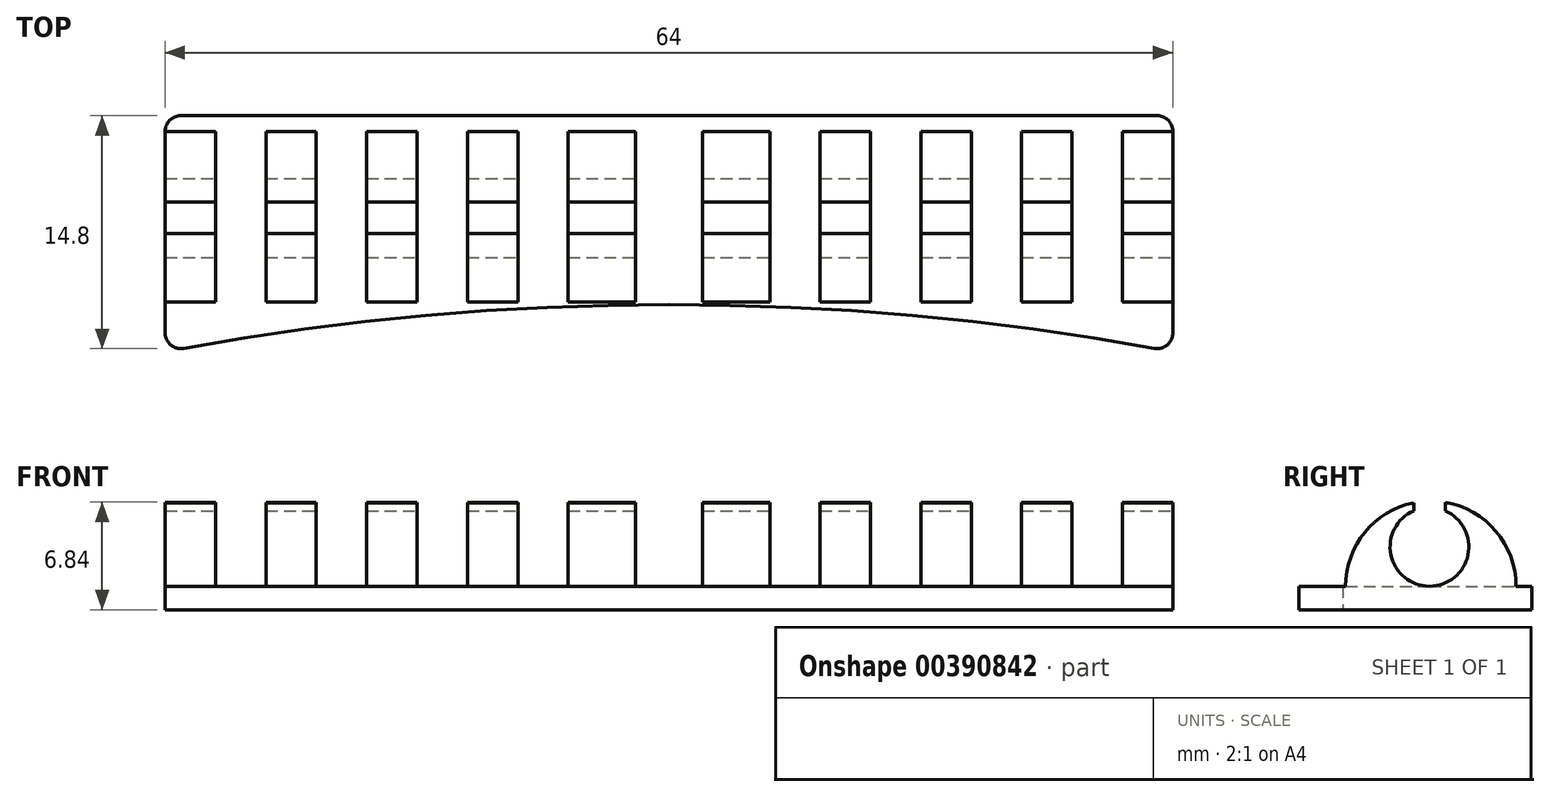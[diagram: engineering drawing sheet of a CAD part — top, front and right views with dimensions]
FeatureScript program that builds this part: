
annotation { "Feature Type Name" : "Feature", "Feature Type Description" : "" }
export const myFeature = defineFeature(function(context is Context, id is Id, definition is map)
    precondition{}
    {
        {
            var Q0;
            Q0=qCreatedBy(makeId("Top.planeOp"),FACE);
            var sketch = newSketch(context, id + "F0", { "sketchPlane" : qUnion([Q0])});
            skLineSegment(sketch, "E0.top", {"start": v(-32, 7.5) * mm, "end": v(32, 7.5) * mm});
            skLineSegment(sketch, "E0.left", {"start": v(-32, -7.5) * mm, "end": v(-32, 7.5) * mm});
            skLineSegment(sketch, "E0.right", {"start": v(32, -7.5) * mm, "end": v(32, 7.5) * mm});
            skPoint(sketch, "E0.middle", {"position": v(0, 0) * mm});
            skArc(sketch, "E1", {"start": v(32, -7.5) * mm, "mid": v(0, -4.5) * mm, "end": v(-32, -7.5) * mm});
            skSolve(sketch);
        }
        {
            var Q0;
            Q0 = qSketchRegion(id + "F0", true);
            extrude(context, id + "F1", {"entities" : qUnion([Q0]), "depth" : 1.5 * mm});
        }
        {
            var Q0;
            Q0=makeQuery(id+"F1.opExtrude","SWEPT_EDGE",EDGE,{"disambiguationData":[OSD([sQuery(id+"F0.wireOp",EDGE,"E0.top"),sQuery(id+"F0.wireOp",EDGE,"E0.right")])]});
            var Q1;
            Q1=makeQuery(id+"F1.opExtrude","SWEPT_EDGE",EDGE,{"disambiguationData":[OSD([sQuery(id+"F0.wireOp",EDGE,"E0.right"),sQuery(id+"F0.wireOp",EDGE,"E1")])]});
            var Q2;
            Q2=makeQuery(id+"F1.opExtrude","SWEPT_EDGE",EDGE,{"disambiguationData":[OSD([sQuery(id+"F0.wireOp",EDGE,"E0.left"),sQuery(id+"F0.wireOp",EDGE,"E1")])]});
            var Q3;
            Q3=makeQuery(id+"F1.opExtrude","SWEPT_EDGE",EDGE,{"disambiguationData":[OSD([sQuery(id+"F0.wireOp",EDGE,"E0.top"),sQuery(id+"F0.wireOp",EDGE,"E0.left")])]});
            fillet(context, id + "F2", {"entities" : qUnion([Q0, Q1, Q2, Q3]), "radius" : 1 * mm, "tangentPropagation" : true, "allowEdgeOverflow" : false});
        }
        {
            var Q0;
            Q0=makeQuery(id+"F1.opExtrude","SWEPT_FACE",FACE,{"disambiguationData":[OSD([sQuery(id+"F0.wireOp",EDGE,"E0.right")])]});
            var sketch = newSketch(context, id + "F3", { "sketchPlane" : qUnion([Q0])});
            skArc(sketch, "E2", {"start": v(0, 6.3) * mm, "mid": v(1, 1.5) * mm, "end": v(2, 6.3) * mm});
            skArc(sketch, "E3", {"start": v(6.5, 1.5) * mm, "mid": v(5.22, 5) * mm, "end": v(2, 6.84) * mm});
            skArc(sketch, "E4", {"start": v(0, 6.8) * mm, "mid": v(-3.1, 4.92) * mm, "end": v(-4.33, 1.5) * mm});
            skLineSegment(sketch, "E5.left", {"start": v(0, 6.3) * mm, "end": v(0, 6.8) * mm});
            skLineSegment(sketch, "E5.right", {"start": v(2, 6.3) * mm, "end": v(2, 6.84) * mm});
            skSolve(sketch);
        }
        {
            var Q0;
            {var subQ4=sQuery(id+"F3.wireOp",EDGE,"E4");Q0=makeQuery(id+"F3.imprint","IMPRINT",FACE,{"disambiguationData":[TD([[makeQuery(id+"F3.imprint","IMPRINT",EDGE,{"derivedFrom":subQ4}),1.0]])]});}
            var Q1;
            {var subQ5=sQuery(id+"F3.wireOp",EDGE,"E3");Q1=makeQuery(id+"F3.imprint","IMPRINT",FACE,{"disambiguationData":[TD([[makeQuery(id+"F3.imprint","IMPRINT",EDGE,{"derivedFrom":subQ5}),1.0]])]});}
            extrude(context, id + "F4", {"entities" : qUnion([Q0, Q1]), "operationType" : NewBodyOperationType.ADD, "oppositeDirection" : true, "depth" : 64 * mm});
        }
        {
            var Q0;
            {var subQ0=sQuery(id+"F0.wireOp",EDGE,"E1");var subQ1=sQuery(id+"F0.wireOp",EDGE,"E0.right");var subQ2=sQuery(id+"F0.wireOp",EDGE,"E0.left");Q0=makeQuery(id+"F4.boolean.opBoolean","SPLIT",FACE,{"disambiguationData":[TD([makeQuery(id+"F1.opExtrude","SWEPT_FACE",FACE,{"disambiguationData":[OSD([subQ0])]})])],"derivedFrom":makeQuery(id+"F1.opExtrude","CAP_FACE",FACE,{"disambiguationData":[OSD([sQuery(id+"F0.wireOp",EDGE,"E0.top"),subQ2,subQ1,subQ0])],"isStart":false})});}
            var sketch = newSketch(context, id + "F5", { "sketchPlane" : qUnion([Q0])});
            skLineSegment(sketch, "E6.bottom", {"start": v(-32, -4.33) * mm, "end": v(32, -4.33) * mm});
            skLineSegment(sketch, "E6.top", {"start": v(-32, 9.34) * mm, "end": v(32, 9.34) * mm});
            skLineSegment(sketch, "E6.left", {"start": v(-32, -4.33) * mm, "end": v(-32, 9.34) * mm});
            skLineSegment(sketch, "E6.right", {"start": v(32, -4.33) * mm, "end": v(32, 9.34) * mm});
            skLineSegment(sketch, "E7", {"start": v(28.8, -4.33) * mm, "end": v(28.8, 9.34) * mm});
            skLineSegment(sketch, "E8", {"start": v(25.6, -4.33) * mm, "end": v(25.6, 9.34) * mm});
            skLineSegment(sketch, "E9", {"start": v(22.4, -4.33) * mm, "end": v(22.4, 9.34) * mm});
            skLineSegment(sketch, "E10", {"start": v(19.2, -4.33) * mm, "end": v(19.2, 9.34) * mm});
            skLineSegment(sketch, "E11", {"start": v(16, -4.33) * mm, "end": v(16, 9.34) * mm});
            skLineSegment(sketch, "E12", {"start": v(12.8, -4.33) * mm, "end": v(12.8, 9.34) * mm});
            skLineSegment(sketch, "E13", {"start": v(9.6, -4.33) * mm, "end": v(9.6, 9.34) * mm});
            skLineSegment(sketch, "E14", {"start": v(6.4, 9.34) * mm, "end": v(6.4, -4.33) * mm});
            skLineSegment(sketch, "E15", {"start": v(-6.4, -4.33) * mm, "end": v(-6.4, 9.34) * mm});
            skLineSegment(sketch, "E16", {"start": v(-9.6, 9.34) * mm, "end": v(-9.6, -4.33) * mm});
            skLineSegment(sketch, "E17", {"start": v(-12.8, 9.34) * mm, "end": v(-12.8, -4.33) * mm});
            skLineSegment(sketch, "E18", {"start": v(-16, 9.34) * mm, "end": v(-16, -4.33) * mm});
            skLineSegment(sketch, "E19", {"start": v(-19.2, 9.34) * mm, "end": v(-19.2, -4.33) * mm});
            skLineSegment(sketch, "E20", {"start": v(-22.4, -4.33) * mm, "end": v(-22.4, 9.34) * mm});
            skLineSegment(sketch, "E21", {"start": v(-25.6, 9.34) * mm, "end": v(-25.6, -4.33) * mm});
            skLineSegment(sketch, "E22", {"start": v(-28.8, -4.33) * mm, "end": v(-28.8, 9.34) * mm});
            skLineSegment(sketch, "E23", {"start": v(-2.13, 9.34) * mm, "end": v(-2.13, -4.33) * mm});
            skLineSegment(sketch, "E24", {"start": v(-6.4, 9.34) * mm, "end": v(-6.4, -4.33) * mm});
            skLineSegment(sketch, "E25", {"start": v(2.13, -4.33) * mm, "end": v(2.13, 9.34) * mm});
            skSolve(sketch);
        }
        {
            var Q0;
            {var subQ0=sQuery(id+"F5.wireOp",EDGE,"E23");Q0=makeQuery(id+"F5.imprint","IMPRINT",FACE,{"disambiguationData":[TD([[makeQuery(id+"F5.imprint","IMPRINT",EDGE,{"derivedFrom":subQ0}),1.0]])]});}
            var Q1;
            {var subQ0=sQuery(id+"F5.wireOp",EDGE,"E16");Q1=makeQuery(id+"F5.imprint","IMPRINT",FACE,{"disambiguationData":[TD([[makeQuery(id+"F5.imprint","IMPRINT",EDGE,{"derivedFrom":subQ0}),1.0]])]});}
            var Q2;
            {var subQ0=sQuery(id+"F5.wireOp",EDGE,"E17");Q2=makeQuery(id+"F5.imprint","IMPRINT",FACE,{"disambiguationData":[TD([[makeQuery(id+"F5.imprint","IMPRINT",EDGE,{"derivedFrom":subQ0}),-1.0]])]});}
            var Q3;
            {var subQ0=sQuery(id+"F5.wireOp",EDGE,"E19");Q3=makeQuery(id+"F5.imprint","IMPRINT",FACE,{"disambiguationData":[TD([[makeQuery(id+"F5.imprint","IMPRINT",EDGE,{"derivedFrom":subQ0}),-1.0]])]});}
            var Q4;
            {var subQ0=sQuery(id+"F5.wireOp",EDGE,"E21");Q4=makeQuery(id+"F5.imprint","IMPRINT",FACE,{"disambiguationData":[TD([[makeQuery(id+"F5.imprint","IMPRINT",EDGE,{"derivedFrom":subQ0}),-1.0]])]});}
            var Q5;
            {var subQ0=sQuery(id+"F5.wireOp",EDGE,"E13");Q5=makeQuery(id+"F5.imprint","IMPRINT",FACE,{"disambiguationData":[TD([[makeQuery(id+"F5.imprint","IMPRINT",EDGE,{"derivedFrom":subQ0}),1.0]])]});}
            var Q6;
            {var subQ0=sQuery(id+"F5.wireOp",EDGE,"E11");Q6=makeQuery(id+"F5.imprint","IMPRINT",FACE,{"disambiguationData":[TD([[makeQuery(id+"F5.imprint","IMPRINT",EDGE,{"derivedFrom":subQ0}),1.0]])]});}
            var Q7;
            {var subQ0=sQuery(id+"F5.wireOp",EDGE,"E9");Q7=makeQuery(id+"F5.imprint","IMPRINT",FACE,{"disambiguationData":[TD([[makeQuery(id+"F5.imprint","IMPRINT",EDGE,{"derivedFrom":subQ0}),1.0]])]});}
            var Q8;
            {var subQ0=sQuery(id+"F5.wireOp",EDGE,"E7");Q8=makeQuery(id+"F5.imprint","IMPRINT",FACE,{"disambiguationData":[TD([[makeQuery(id+"F5.imprint","IMPRINT",EDGE,{"derivedFrom":subQ0}),1.0]])]});}
            extrude(context, id + "F6", {"entities" : qUnion([Q0, Q1, Q2, Q3, Q4, Q5, Q6, Q7, Q8]), "operationType" : NewBodyOperationType.REMOVE, "depth" : 7.72 * mm});
        }
    });
